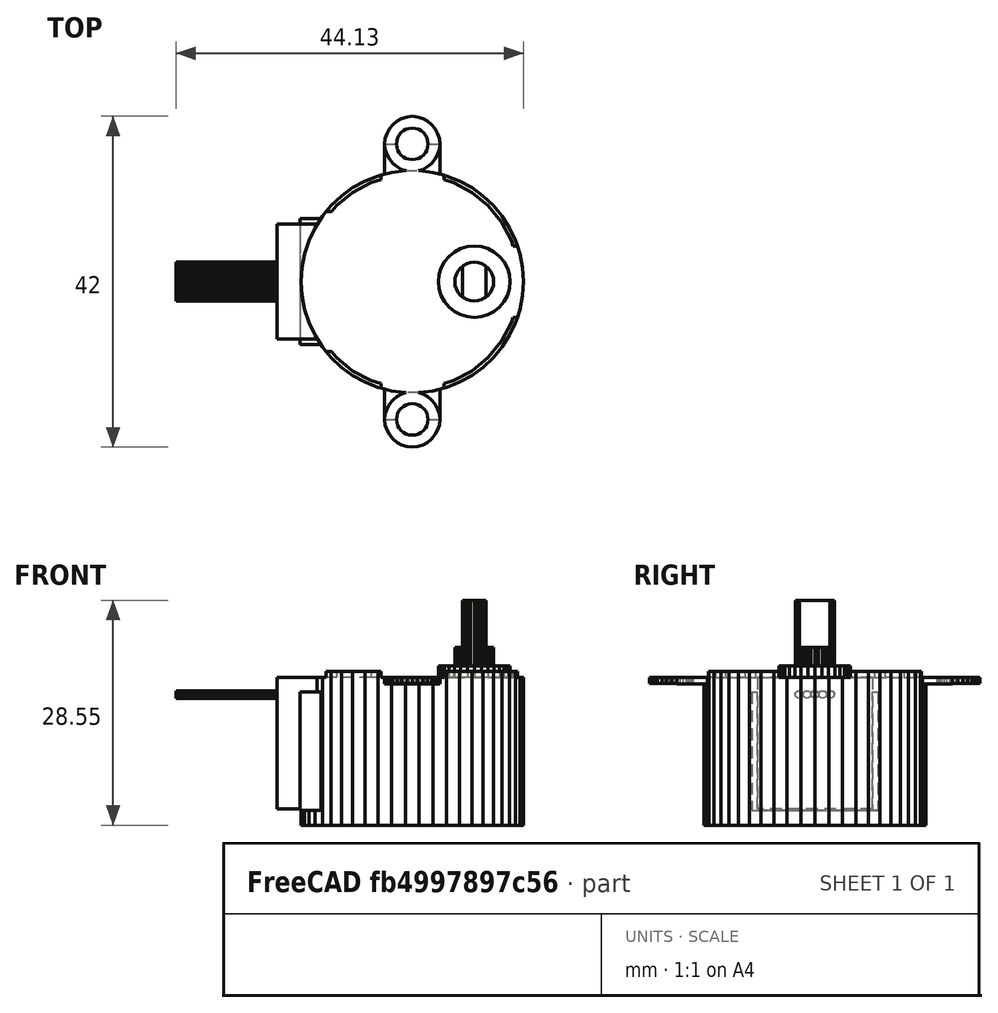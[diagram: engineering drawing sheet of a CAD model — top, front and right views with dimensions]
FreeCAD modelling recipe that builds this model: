
FCSTD DOCUMENT  (FreeCAD 0.14R3692 (Git))
Label: stepper-motor
License: The MIT License
LicenseURL: http://opensource.org/licenses/MIT
objects: Part::Prism×14, Part::Box×8, Part::MultiFuse×3, Part::Cut×3, Part::Fuse×3, Part::Feature×1
note: 32 computed .brp shape members not serialized (recipe doc carries the construction recipe); baked Part::Feature solids carry a one-line shape summary decoded from their .brp

FEATURE [Part::Prism] prism
  Circumradius = 14.125
  Height = 0.75
  Placement = pos=(0,0,-0.375) rot=(0,0,1;0rad)
  Polygon = 50
FEATURE [Part::Prism] prism001
  Circumradius = 13.625
  Height = 0.8
  Placement = pos=(0,0,-0.4) rot=(0,0,1;0rad)
  Polygon = 32
FEATURE [Part::Box] cube
  Height = 1.4
  Length = 8
  Placement = pos=(-4,-17.5,-0.7) rot=(0,0,1;0rad)
  Width = 35
FEATURE [Part::Box] cube001
  Height = 1.4
  Length = 30.25
  Placement = pos=(-15.125,-4.55,-0.7) rot=(0,0,1;0rad)
  Width = 9.1
FEATURE [Part::Box] cube002
  Height = 1.4
  Length = 28.25
  Placement = pos=(-28.25,-8.9,-0.7) rot=(0,0,1;0rad)
  Width = 17.8
FEATURE [Part::MultiFuse] union
  Shapes = -> [prism001,cube,cube001,cube002]
FEATURE [Part::Cut] difference
  Base = -> prism
  Placement = pos=(0,0,-9.75) rot=(0,0,1;0rad)
  Tool = -> union
FEATURE [Part::Prism] prism002
  Circumradius = 14.125
  Height = 18.8
  Placement = pos=(0,0,-9.4) rot=(0,0,1;0rad)
  Polygon = 50
FEATURE [Part::Prism] prism003
  Circumradius = 4.55
  Height = 18.8
  Placement = pos=(7.875,0,-10.85) rot=(0,0,1;0rad)
  Polygon = 32
FEATURE [Part::Prism] prism004
  Circumradius = 2.465
  Height = 18.8
  Placement = pos=(0,0,-9.4) rot=(0,0,1;0rad)
  Polygon = 32
FEATURE [Part::Box] cube003
  Height = 6
  Length = 4.93
  Placement = pos=(1.5,-2.465,-9.425) rot=(0,0,1;0rad)
  Width = 4.93
FEATURE [Part::Box] cube004
  Height = 6
  Length = 4.93
  Placement = pos=(-6.43,-2.465,-9.425) rot=(0,0,1;0rad)
  Width = 4.93
FEATURE [Part::Fuse] union001
  Base = -> cube003
  Tool = -> cube004
FEATURE [Part::Cut] difference001
  Base = -> prism004
  Placement = pos=(7.875,0,-9.75) rot=(0,0,1;0rad)
  Tool = -> union001
FEATURE [Part::Box] cube005
  Height = 0.8
  Length = 7
  Placement = pos=(-3.5,-17.5,-9.375) rot=(0,0,1;0rad)
  Width = 35
FEATURE [Part::Prism] prism005
  Circumradius = 3.5
  Height = 0.8
  Placement = pos=(0,17.5,-9.4) rot=(0,0,1;0rad)
  Polygon = 32
FEATURE [Part::Prism] prism006
  Circumradius = 3.5
  Height = 0.8
  Placement = pos=(0,-17.5,-9.4) rot=(0,0,1;0rad)
  Polygon = 32
FEATURE [Part::Box] cube006
  Height = 16.7
  Length = 28.25
  Placement = pos=(-17.175,-7.3,-9.35) rot=(0,0,1;0rad)
  Width = 14.6
FEATURE [Part::Box] cube007
  Height = 15
  Length = 24.5
  Placement = pos=(-14.25,-8,-7.5) rot=(0,0,1;0rad)
  Width = 16
FEATURE [Part::MultiFuse] union002
  Shapes = -> [difference,prism002,prism003,difference001,cube005,prism005,prism006,cube006,cube007]
FEATURE [Part::Prism] prism007
  Circumradius = 2
  Height = 2
  Placement = pos=(0,17.5,-10.4) rot=(0,0,1;0rad)
  Polygon = 32
FEATURE [Part::Prism] prism008
  Circumradius = 2
  Height = 2
  Placement = pos=(0,-17.5,-10.4) rot=(0,0,1;0rad)
  Polygon = 32
FEATURE [Part::Fuse] union003
  Base = -> prism007
  Tool = -> prism008
FEATURE [Part::Cut] difference002
  Base = -> union002
  Tool = -> union003
FEATURE [Part::Prism] prism009 .. prism013  x5 (patterned run collapsed; names and placements below)
  Circumradius = 0.5
  Height = 30
  Polygon = 7
  placements: 5 in arithmetic series — first pos=(0,2,0) rot=(0,0,1;0rad), step (0,-1,0), last pos=(0,-2,0) rot=(0,0,1;0rad)
FEATURE [Part::MultiFuse] Group
  Placement = pos=(0,0,-7.2) rot=(0,-1,0;1.5708rad)
  Shapes = -> [prism009,prism010,prism011,prism012,prism013]
FEATURE [Part::Fuse] Matrix_Union
  Base = -> difference002
  Placement = pos=(0,0,0) rot=(1,0,0;3.14159rad)
  Tool = -> Group
FEATURE [Part::Feature] Matrix_Union001  label="stepper-motor"
  Placement = pos=(0,0,0) rot=(1,0,0;3.14159rad)
  shape: bbox 44.13 x 42 x 28.55 mm, 425 faces (baked)
